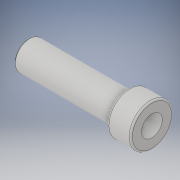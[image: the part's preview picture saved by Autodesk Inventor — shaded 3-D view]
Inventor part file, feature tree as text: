
AUTODESK INVENTOR PART (.ipt)
format: ipt  version: 2018.3 (Build 223284000, 284)  size: 139,776 bytes
history: native  units: in
note: dims shown in document units (in); Inventor stores cm internally (conversion verified against a paired STEP export)
features: fillet x2, revolve x1, sketch x1
ambient origin geometry x8: Origin, YZ Plane, XZ Plane, XY Plane, X Axis, Y Axis, Z Axis, Center Point
bodies: Solid1 (feature_tree)
feature tree (4):
  revolve  "Revolution1"  [1 undecoded]
  fillet  "Fillet1"  Radius=0.142in
  fillet  "Fillet2"  Radius=0.063in
  sketch  "Sketch1"  dims[d0=0.75in d1=0.087in d2=0.142in d3=0.063in d4=45.0deg d5=0.01in d6=0.01in d7=90.0deg d8=0.02in d9=0.01in]
note: 1 required parameter value undecoded (feature->parameter linkage not recoverable at this tier; creation-order binding heuristic only, values carry confidence <= 0.55)
